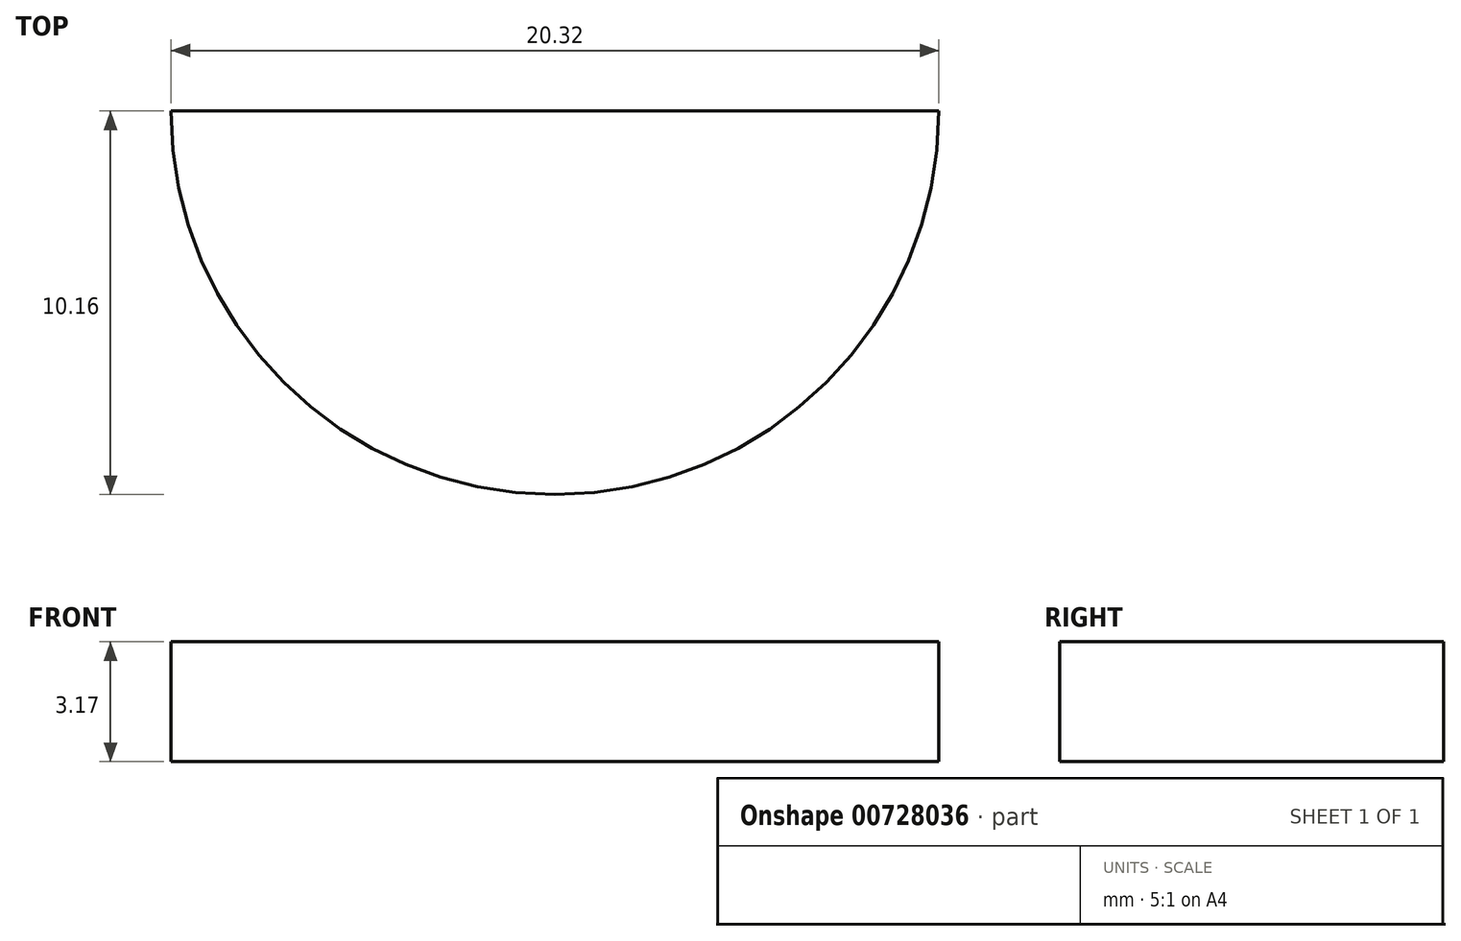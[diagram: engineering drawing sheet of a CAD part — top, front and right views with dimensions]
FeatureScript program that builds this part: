
annotation { "Feature Type Name" : "Feature", "Feature Type Description" : "" }
export const myFeature = defineFeature(function(context is Context, id is Id, definition is map)
    precondition{}
    {
        {
            var Q0;
            Q0=qCreatedBy(makeId("Top.planeOp"),FACE);
            var sketch = newSketch(context, id + "F0", { "sketchPlane" : qUnion([Q0])});
            skArc(sketch, "E0", {"start": v(-10.16, 0) * mm, "mid": v(0, -10.16) * mm, "end": v(10.16, 0) * mm});
            skLineSegment(sketch, "E1", {"start": v(-10.16, 0) * mm, "end": v(10.16, 0) * mm});
            skSolve(sketch);
        }
        {
            var Q0;
            Q0 = qSketchRegion(id + "F0", true);
            extrude(context, id + "F1", {"entities" : qUnion([Q0]), "depth" : 3.17 * mm, "offsetDistance" : 25.4 * mm});
        }
    });
